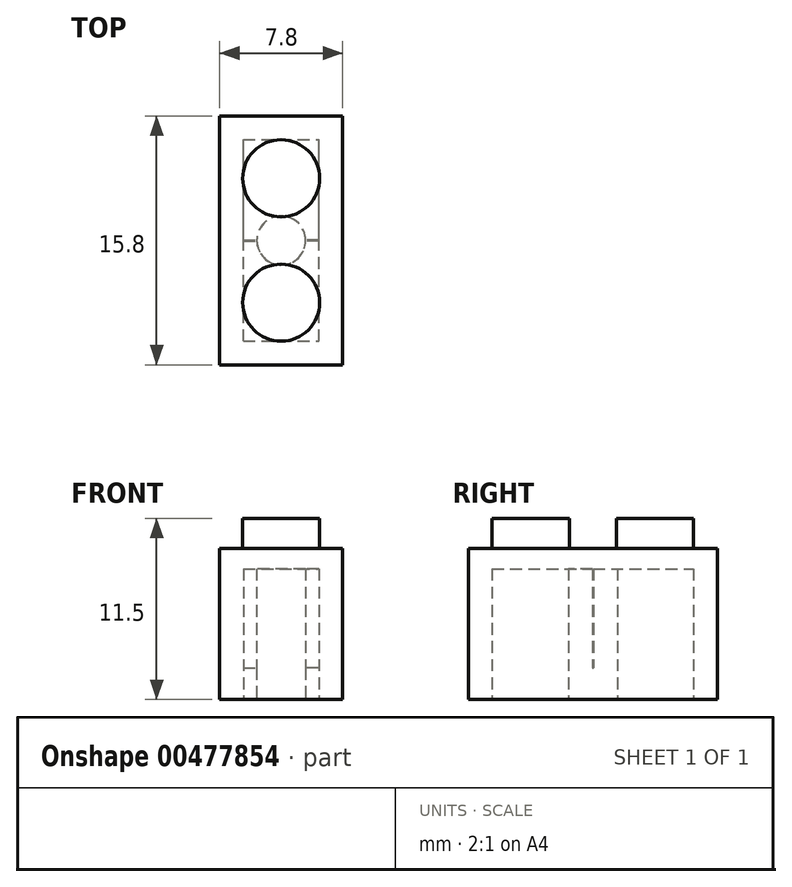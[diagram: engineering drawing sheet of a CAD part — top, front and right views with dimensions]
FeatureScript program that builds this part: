
annotation { "Feature Type Name" : "Feature", "Feature Type Description" : "" }
export const myFeature = defineFeature(function(context is Context, id is Id, definition is map)
    precondition{}
    {
        {
            var Q0;
            Q0=qCreatedBy(makeId("Top.planeOp"),FACE);
            var sketch = newSketch(context, id + "F0", { "sketchPlane" : qUnion([Q0])});
            skLineSegment(sketch, "E0", {"start": v(-61.37, 40.7) * mm, "end": v(-61.37, 24.9) * mm});
            skLineSegment(sketch, "E1", {"start": v(-61.37, 40.7) * mm, "end": v(-53.57, 40.7) * mm});
            skLineSegment(sketch, "E2", {"start": v(-53.57, 40.7) * mm, "end": v(-53.57, 24.9) * mm});
            skLineSegment(sketch, "E3", {"start": v(-53.57, 24.9) * mm, "end": v(-61.37, 24.9) * mm});
            skSolve(sketch);
        }
        {
            var Q0;
            Q0=qCreatedBy(makeId("Front.planeOp"),FACE);
            var sketch = newSketch(context, id + "F1", { "sketchPlane" : qUnion([Q0])});
            skSolve(sketch);
        }
        {
            var Q0;
            Q0 = qSketchRegion(id + "F1", true);
            var Q1;
            Q1=makeQuery(id+"F0.imprint","IMPRINT",FACE,{"disambiguationData":[TD([[makeQuery(id+"F0.imprint","IMPRINT",EDGE,{"derivedFrom":sQuery(id+"F0.wireOp",EDGE,"E0")}),1.0]])]});
            extrude(context, id + "F2", {"entities" : qUnion([Q0, Q1]), "depth" : 9.6 * mm});
        }
        {
            var Q0;
            Q0=makeQuery(id+"F2.opExtrude","CAP_FACE",FACE,{"disambiguationData":[OSD([sQuery(id+"F0.wireOp",EDGE,"E0"),sQuery(id+"F0.wireOp",EDGE,"E1"),sQuery(id+"F0.wireOp",EDGE,"E2"),sQuery(id+"F0.wireOp",EDGE,"E3")])],"isStart":false});
            var sketch = newSketch(context, id + "F3", { "sketchPlane" : qUnion([Q0])});
            skLineSegment(sketch, "E4", {"start": v(-57.47, 40.7) * mm, "end": v(-57.47, 24.9) * mm, "construction": true});
            skLineSegment(sketch, "E5", {"start": v(-61.37, 32.8) * mm, "end": v(-61.37, 40.7) * mm, "construction": true});
            skLineSegment(sketch, "E6", {"start": v(-61.37, 36.76) * mm, "end": v(-53.57, 36.76) * mm, "construction": true});
            skCircle(sketch, "E7", {"center": v(-57.47, 36.76) * mm, "radius": 2.45 * mm});
            skLineSegment(sketch, "E8.MirrorCS", {"start": v(-61.37, 40.7) * mm, "end": v(-53.57, 40.7) * mm, "construction": true});
            skLineSegment(sketch, "E9.MirrorCS", {"start": v(-57.47, 32.8) * mm, "end": v(-57.47, 48.6) * mm, "construction": true});
            skLineSegment(sketch, "E10.MirrorCS", {"start": v(-61.37, 40.7) * mm, "end": v(-61.37, 32.8) * mm, "construction": true});
            skLineSegment(sketch, "E11", {"start": v(-61.37, 32.8) * mm, "end": v(-53.57, 32.8) * mm});
            skCircle(sketch, "E12.MirrorC", {"center": v(-57.47, 28.86) * mm, "radius": 2.45 * mm});
            skSolve(sketch);
        }
        {
            var Q0;
            Q0 = qSketchRegion(id + "F3", true);
            extrude(context, id + "F4", {"entities" : qUnion([Q0]), "operationType" : NewBodyOperationType.ADD, "depth" : 1.9 * mm});
        }
        {
            var Q0;
            Q0=makeQuery(id+"F2.opExtrude","CAP_FACE",FACE,{"disambiguationData":[OSD([sQuery(id+"F0.wireOp",EDGE,"E0"),sQuery(id+"F0.wireOp",EDGE,"E1"),sQuery(id+"F0.wireOp",EDGE,"E2"),sQuery(id+"F0.wireOp",EDGE,"E3")])],"isStart":true});
            var sketch = newSketch(context, id + "F5", { "sketchPlane" : qUnion([Q0])});
            skLineSegment(sketch, "E13.bottom", {"start": v(-59.87, -26.4) * mm, "end": v(-55.07, -26.4) * mm});
            skLineSegment(sketch, "E13.top", {"start": v(-59.87, -39.2) * mm, "end": v(-55.07, -39.2) * mm});
            skLineSegment(sketch, "E13.left", {"start": v(-59.87, -26.4) * mm, "end": v(-59.87, -39.2) * mm});
            skLineSegment(sketch, "E13.right", {"start": v(-55.07, -26.4) * mm, "end": v(-55.07, -39.2) * mm});
            skCircle(sketch, "E14", {"center": v(-57.47, -32.8) * mm, "radius": 1.55 * mm});
            skLineSegment(sketch, "E15", {"start": v(-55.07, -32.83) * mm, "end": v(-55.92, -32.83) * mm});
            skLineSegment(sketch, "E16", {"start": v(-55.07, -32.78) * mm, "end": v(-55.92, -32.78) * mm});
            skLineSegment(sketch, "E17", {"start": v(-59.87, -32.83) * mm, "end": v(-59.02, -32.83) * mm});
            skLineSegment(sketch, "E18", {"start": v(-59.87, -32.78) * mm, "end": v(-59.02, -32.78) * mm});
            skSolve(sketch);
        }
        {
            var Q0;
            Q0=makeQuery(id+"F5.imprint","IMPRINT",FACE,{"disambiguationData":[TD([[makeQuery(id+"F5.imprint","IMPRINT",EDGE,{"derivedFrom":sQuery(id+"F5.wireOp",EDGE,"E13.bottom")}),-1.0]])]});
            extrude(context, id + "F6", {"entities" : qUnion([Q0]), "operationType" : NewBodyOperationType.REMOVE, "oppositeDirection" : true, "depth" : 8.3 * mm});
        }
        {
            var Q0;
            Q0 = qSketchRegion(id + "F5", true);
            extrude(context, id + "F7", {"entities" : qUnion([Q0]), "operationType" : NewBodyOperationType.REMOVE, "oppositeDirection" : true, "depth" : 8.3 * mm});
        }
        {
            var Q0;
            {var subQ0=sQuery(id+"F5.wireOp",EDGE,"E15");Q0=makeQuery(id+"F5.imprint","IMPRINT",FACE,{"disambiguationData":[TD([[makeQuery(id+"F5.imprint","IMPRINT",EDGE,{"derivedFrom":subQ0}),-1.0]])]});}
            var Q1;
            Q1=sQuery(id+"F5.wireOp",EDGE,"E16");
            var Q2;
            Q2=sQuery(id+"F5.wireOp",EDGE,"E15");
            extrude(context, id + "F8", {"entities" : qUnion([Q0]), "operationType" : NewBodyOperationType.ADD, "surfaceEntities" : qUnion([Q1, Q2]), "oppositeDirection" : true, "depth" : 8.3 * mm});
        }
        {
            var Q0;
            {var subQ0=sQuery(id+"F5.wireOp",EDGE,"E17");Q0=makeQuery(id+"F5.imprint","IMPRINT",FACE,{"disambiguationData":[TD([[makeQuery(id+"F5.imprint","IMPRINT",EDGE,{"derivedFrom":subQ0}),1.0]])]});}
            extrude(context, id + "F9", {"entities" : qUnion([Q0]), "operationType" : NewBodyOperationType.ADD, "oppositeDirection" : true, "depth" : 8.3 * mm});
        }
        {
            var Q0;
            {var subQ0=sQuery(id+"F5.wireOp",EDGE,"E17");Q0=makeQuery(id+"F5.imprint","IMPRINT",FACE,{"disambiguationData":[TD([[makeQuery(id+"F5.imprint","IMPRINT",EDGE,{"derivedFrom":subQ0}),1.0]])]});}
            extrude(context, id + "F10", {"entities" : qUnion([Q0]), "operationType" : NewBodyOperationType.REMOVE, "oppositeDirection" : true, "depth" : 2 * mm});
        }
        {
            var Q0;
            {var subQ0=sQuery(id+"F5.wireOp",EDGE,"E15");Q0=makeQuery(id+"F5.imprint","IMPRINT",FACE,{"disambiguationData":[TD([[makeQuery(id+"F5.imprint","IMPRINT",EDGE,{"derivedFrom":subQ0}),-1.0]])]});}
            extrude(context, id + "F11", {"entities" : qUnion([Q0]), "operationType" : NewBodyOperationType.REMOVE, "oppositeDirection" : true, "depth" : 2 * mm});
        }
    });
